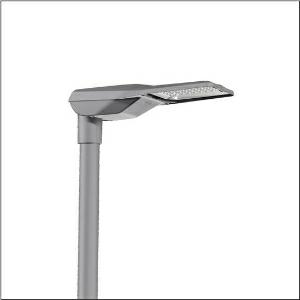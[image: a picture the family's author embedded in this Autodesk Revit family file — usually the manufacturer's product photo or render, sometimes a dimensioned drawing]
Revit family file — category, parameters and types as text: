
# Revit family: streetlight_sl_21_iq_mini___p1_0a_5xe2a41d08hb_633f
name_source: partatom
category: Lighting Fixtures
units: mm (PartAtom-declared; Revit-internal decimal feet)

## family parameters
Cut with Voids When Loaded = No
Host = Face
Light Source = No
Part Type = Normal
Room Calculation Point = No
Round Connector Dimension = Use Diameter
Shared = No

## types (1)
- --- (1 x LED, 9860 lm, 70.9 W, 4000K)
    Apparent Load = 71 VA
    CIE Flux Codes = 21 50 90 100 100
    Color Rendering = 70
    Color Temperature = 4000K
    Default Elevation = 1800 mm
    Description = Streetlight SL 21 iQ mini, mast luminaire, primary light control with lens, of PMMA, primary optical cover: cover, of toughened safety glass, transparent, light distribution: P1.0a, light emission: direct distribution, primary light characteristic: asymmetric, installation type: post-top, side-entry, LED, High Power LED, rated luminous flux: 9.860lm, luminous efficacy: 139lm/W, light colour: 740, colour temperature: 4000K, control gear: iQ-Comfort, control: Auto-Match, Temp-Guard, Lumen-Switch, Night-Set, Smart-Wire, Light-Fading, Desk-Remote (wireless, voltage-free reading and setting of iQ features in the workshop via application-optimized NFC function/RFID function), optimised constant luminous flux control (CLO 2.0), pre-setting: linear dimming characteristic, mains connection: 220..240V, AC, 50/60Hz, start of lifetime: 71W, end of service life: 75W, reduction: 31W, luminaire housing, of diecast aluminium, powder-coated, Siteco® metallic grey (DB 702S), corrosivity category C5 mid according to DIN EN ISO 12944, please order mast flange separately, inclination adjustable: 0°, 5°, 10°, 15°, sealing non-destructively replaceable, multi-level sealing system, length: 628mm, width: 235mm, height: 110mm, mast flange for spigot size: 42mm (side-entry): 5XC10008XM4, 60/48mm (side-entry/post-top): 5XC10108XM2, 76/60mm (side-entry/post-top): 5XC10108XM1, mounting height: 4..8m, protection rating (complete): IP66, insulation class (complete): insulation class II (safety insulation), certification: CE, ENEC, ENEC+, VDE, impact resistance: IK10, permissible operating ambient temperature for outdoor applications: -40..+50°C, standard-compliant lighting for roads and squares, packaging unit: 1 piece

Light Distribution: P1.0a
    Height = 110 mm
    Lamp = 1 x LED
    Lamp Light Flux = 9860 lm
    Lamp Power = 70.9 W
    Lamp count = 1
    Length = 625 mm
    Luminous efficacy = 139 lm/W
    Manufacturer = Siteco
    ModVariant = No
    Model = 5XE2A41D08HB
    Number of Poles = 1
    OnlyDefault = Yes
    Power Factor = 1
    Product Name = Streetlight SL 21 iQ mini | P1.0a
    Product group = mast luminaire | pylon top
    ProductGroupID = 6100
    Protection Class = Protection class II
    Protection Degree = IP 66
    RLX_Detail_Level = 1
    RLX_Emergency_Light_Flux = 0 lm
    RLX_Emergency_Type = 0
    RLX_Emergency_Type_DB = No
    RlxData = <blob elided: 37529 chars, md5=2663ce0f>
    Socket = socket
    Standby Power = 0 W
    System Light Flux = 9860 lm
    System Power = 71 W
    Type Comments = factory setting: luminous flux: 100 % | dim-lin: 254 | 711 mA
    Type Image = l_1003519.jpg
    URL = http://relux.com
    VarID = @adj_157656
    Voltage = 0 V
    Weight = 0.00 kg
    Width = 234 mm

## geometry (parser evidence)
native form markers: Blend x4, Sweep x9
no freeform markers — native parametric forms only
